# Revit family: PRD_FrankeWS_SpDshs_ACCESSOIRESCornerBasket_MISX2009HP
name_source: partatom
category: Specialty Equipment
revit_build: Autodesk Revit 2018 (Build: 20190510_1515(x64)
units: mm (PartAtom-declared; Revit-internal decimal feet)

## family parameters
Cut with Voids When Loaded = No
Host = Face
OmniClass Number = 23.40.20.21.34
OmniClass Title = Soap Holders, Dispensers
Part Type = Normal
Room Calculation Point = No
Round Connector Dimension = Use Diameter
Shared = No

## types (1)
- MISX2009HP
    AssetType = Fixed
    BIMObjectName = PRD_AR_SoapDishes_ACCESSOIRESCornerBasket_MISX2009HP
    BasketMaterial = PRD_AR_StainlessSteel_HighPolished
    Category = Pr_40_20_76_82, Soap dishes
    Default Elevation = 1200 mm
    Description = Corner basket for wall mounting, 304 stainless steel, used for shower or bath, inclusive stainless steel screws and dowels.
    DurationUnit = year
    Features = stainless steel, surface high polished
    Finish = high polished
    GrossWeight = 0.65 kg
    IfcExportAs = IfcFurnitureType
    IfcExportType = USERDEFINED
    IntegralAccessories = incl. stainless steel screws and dowels
    IsBuiltIn = TRUE
    MainColor = stainless steel
    Manufacturer = KWC Group AG
    ManufacturerName = KWC Group AG
    ManufacturerURL = www.kwc.com
    Material = stainless steel
    MaterialCode = 1.4301
    Model = MISX2009HP
    ModelNumber = 2000106380
    ModelReference = MISX2009HP
    NBSDescription = Soap dishes
    NBSReference = 45-35-72/356
    Name = Corner basket MISX2009HP
    NetWeight = 0.44 kg
    NominalDepth = 205 mm  [stored 0.672572 ft]
    NominalHeight = 50 mm  [stored 0.164042 ft]
    NominalWidth = 205 mm  [stored 0.672572 ft]
    ProductInformation = https://pim.kwc.com
    Size = 205 x 50 x 205 mm
    Style = Basket
    TypeOfFixing = Screw
    TypeOfMounting = Wall mounting
    URL = www.kwc.com
    Uniclass2015Code = Pr_40_20_76_82
    Uniclass2015Title = Soap dishes
    Uniclass2015Version = Products v1.17
    Version = 1
    WarrantyDurationUnit = year

note: [stored X ft] marks values corroborated as IEEE doubles in the binary element streams (Revit-internal decimal feet)

## geometry (parser evidence)
native form markers: Sweep x2
no freeform markers — native parametric forms only
